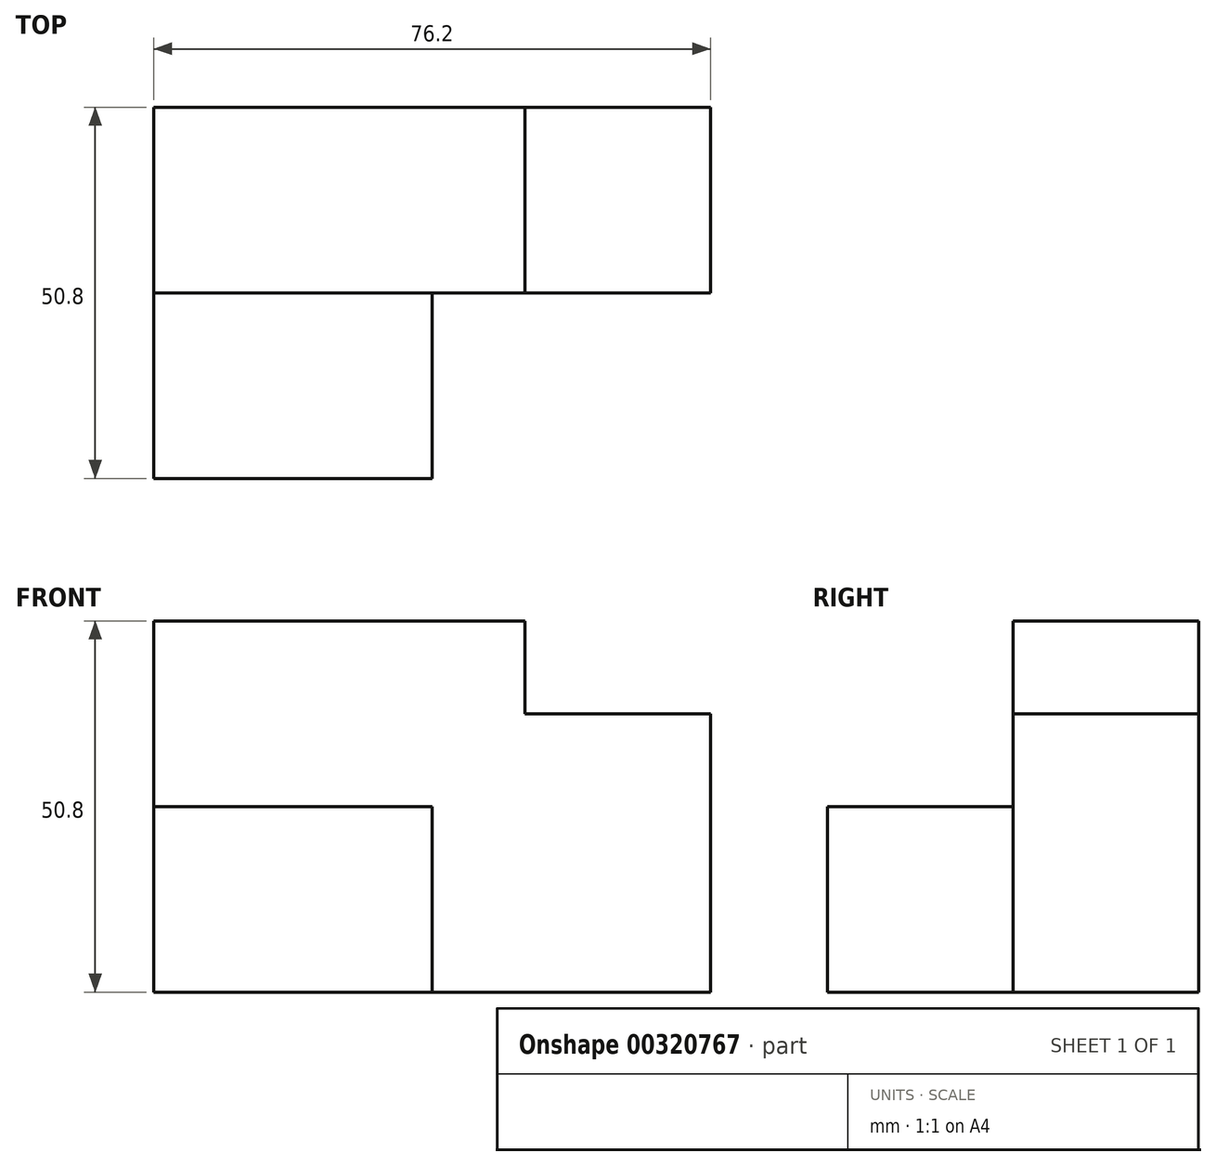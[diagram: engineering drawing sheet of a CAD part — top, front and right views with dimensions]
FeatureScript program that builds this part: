
annotation { "Feature Type Name" : "Feature", "Feature Type Description" : "" }
export const myFeature = defineFeature(function(context is Context, id is Id, definition is map)
    precondition{}
    {
        {
            var Q0;
            Q0=qCreatedBy(makeId("Front.planeOp"),FACE);
            var sketch = newSketch(context, id + "F0", { "sketchPlane" : qUnion([Q0])});
            skLineSegment(sketch, "E0", {"start": v(-57.88, -39.02) * mm, "end": v(-57.88, 11.78) * mm});
            skLineSegment(sketch, "E1", {"start": v(-57.88, 11.78) * mm, "end": v(-7.08, 11.78) * mm});
            skLineSegment(sketch, "E2", {"start": v(-7.08, 11.78) * mm, "end": v(-7.08, -0.92) * mm});
            skLineSegment(sketch, "E3", {"start": v(-7.08, -0.92) * mm, "end": v(18.32, -0.92) * mm});
            skLineSegment(sketch, "E4", {"start": v(18.32, -0.92) * mm, "end": v(18.32, -39.02) * mm});
            skLineSegment(sketch, "E5", {"start": v(18.32, -39.02) * mm, "end": v(-57.88, -39.02) * mm});
            skSolve(sketch);
        }
        {
            var Q0;
            Q0=makeQuery(id+"F0.imprint","IMPRINT",FACE,{"disambiguationData":[TD([[makeQuery(id+"F0.imprint","IMPRINT",EDGE,{"derivedFrom":sQuery(id+"F0.wireOp",EDGE,"E0")}),-1.0]])]});
            extrude(context, id + "F1", {"entities" : qUnion([Q0]), "depth" : 25.4 * mm});
        }
        {
            var Q0;
            Q0=makeQuery(id+"F1.opExtrude","CAP_FACE",FACE,{"disambiguationData":[OSD([sQuery(id+"F0.wireOp",EDGE,"E0"),sQuery(id+"F0.wireOp",EDGE,"E1"),sQuery(id+"F0.wireOp",EDGE,"E2"),sQuery(id+"F0.wireOp",EDGE,"E3"),sQuery(id+"F0.wireOp",EDGE,"E4"),sQuery(id+"F0.wireOp",EDGE,"E5")])],"isStart":false});
            var sketch = newSketch(context, id + "F2", { "sketchPlane" : qUnion([Q0])});
            skLineSegment(sketch, "E6", {"start": v(-19.78, -39.02) * mm, "end": v(-19.78, -13.62) * mm});
            skLineSegment(sketch, "E7", {"start": v(-19.78, -13.62) * mm, "end": v(-57.88, -13.62) * mm});
            skSolve(sketch);
        }
        {
            var Q0;
            {var subQ0=sQuery(id+"F2.wireOp",EDGE,"E6");Q0=makeQuery(id+"F2.imprint","IMPRINT",FACE,{"disambiguationData":[TD([[makeQuery(id+"F2.imprint","IMPRINT",EDGE,{"derivedFrom":subQ0}),1.0]])]});}
            extrude(context, id + "F3", {"entities" : qUnion([Q0]), "operationType" : NewBodyOperationType.ADD, "depth" : 25.4 * mm});
        }
    });
